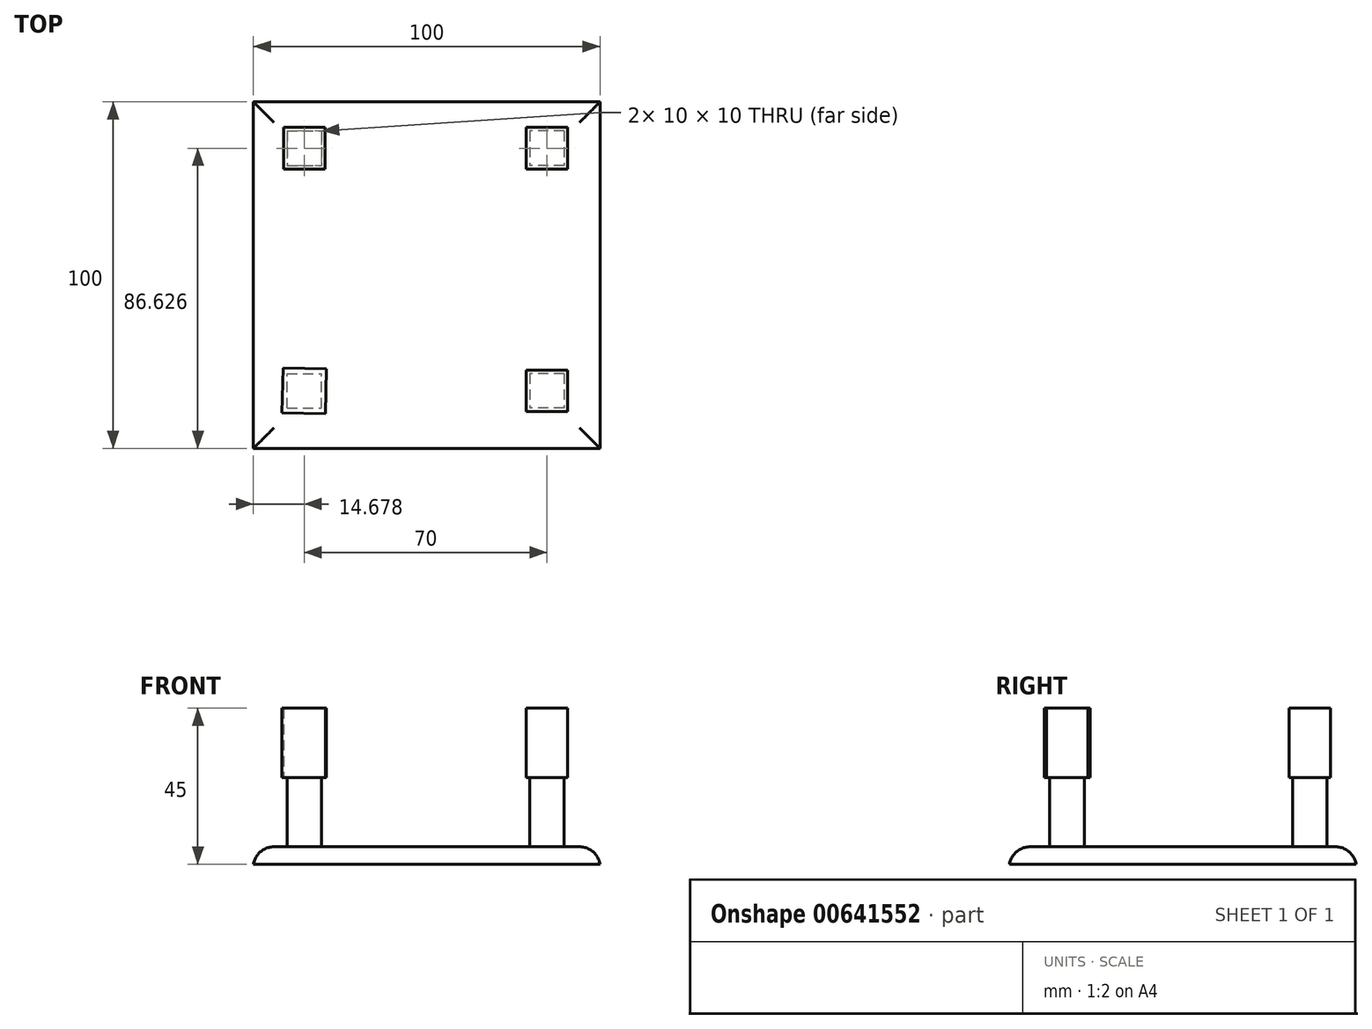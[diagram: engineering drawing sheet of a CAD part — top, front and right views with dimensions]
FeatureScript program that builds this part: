
annotation { "Feature Type Name" : "Feature", "Feature Type Description" : "" }
export const myFeature = defineFeature(function(context is Context, id is Id, definition is map)
    precondition{}
    {
        {
            var Q0;
            Q0=qCreatedBy(makeId("Top.planeOp"),FACE);
            var sketch = newSketch(context, id + "F0", { "sketchPlane" : qUnion([Q0])});
            skLineSegment(sketch, "E0.bottom", {"start": v(0, 0) * mm, "end": v(50, 0) * mm});
            skLineSegment(sketch, "E0.top", {"start": v(0, 50) * mm, "end": v(50, 50) * mm});
            skLineSegment(sketch, "E0.left", {"start": v(0, 0) * mm, "end": v(0, 50) * mm});
            skLineSegment(sketch, "E0.right", {"start": v(50, 0) * mm, "end": v(50, 50) * mm});
            skLineSegment(sketch, "E1.bottom", {"start": v(0, 0) * mm, "end": v(-50, 0) * mm});
            skLineSegment(sketch, "E1.top", {"start": v(0, 50) * mm, "end": v(-50, 50) * mm});
            skLineSegment(sketch, "E1.right", {"start": v(-50, 0) * mm, "end": v(-50, 50) * mm});
            skLineSegment(sketch, "E2.top", {"start": v(0, -50) * mm, "end": v(-50, -50) * mm});
            skLineSegment(sketch, "E2.left", {"start": v(0, 0) * mm, "end": v(0, -50) * mm});
            skLineSegment(sketch, "E2.right", {"start": v(-50, 0) * mm, "end": v(-50, -50) * mm});
            skLineSegment(sketch, "E3.top", {"start": v(0, -50) * mm, "end": v(50, -50) * mm});
            skLineSegment(sketch, "E3.right", {"start": v(50, 0) * mm, "end": v(50, -50) * mm});
            skSolve(sketch);
        }
        {
            var Q0;
            Q0 = qSketchRegion(id + "F0", true);
            extrude(context, id + "F1", {"entities" : qUnion([Q0]), "depth" : 5 * mm, "offsetDistance" : 25 * mm});
        }
        {
            var Q0;
            Q0=makeQuery(id+"F1.opExtrude","CAP_EDGE",EDGE,{"disambiguationData":[OSD([sQuery(id+"F0.wireOp",EDGE,"E1.right"),sQuery(id+"F0.wireOp",EDGE,"E2.right")])],"isStart":false});
            var Q1;
            Q1=makeQuery(id+"F1.opExtrude","CAP_EDGE",EDGE,{"disambiguationData":[OSD([sQuery(id+"F0.wireOp",EDGE,"E0.top"),sQuery(id+"F0.wireOp",EDGE,"E1.top")])],"isStart":false});
            var Q2;
            Q2=makeQuery(id+"F1.opExtrude","CAP_EDGE",EDGE,{"disambiguationData":[OSD([sQuery(id+"F0.wireOp",EDGE,"E0.right"),sQuery(id+"F0.wireOp",EDGE,"E3.right")])],"isStart":false});
            var Q3;
            Q3=makeQuery(id+"F1.opExtrude","CAP_EDGE",EDGE,{"disambiguationData":[OSD([sQuery(id+"F0.wireOp",EDGE,"E2.top"),sQuery(id+"F0.wireOp",EDGE,"E3.top")])],"isStart":false});
            fillet(context, id + "F2", {"entities" : qUnion([Q0, Q1, Q2, Q3]), "radius" : 6 * mm, "tangentPropagation" : true, "allowEdgeOverflow" : false});
        }
        {
            var Q0;
            Q0=qCreatedBy(makeId("Top.planeOp"),FACE);
            var sketch = newSketch(context, id + "F3", { "sketchPlane" : qUnion([Q0])});
            skLineSegment(sketch, "E4.bottom", {"start": v(-30.32, 31.63) * mm, "end": v(-40.32, 31.63) * mm});
            skLineSegment(sketch, "E4.top", {"start": v(-30.32, 41.63) * mm, "end": v(-40.32, 41.63) * mm});
            skLineSegment(sketch, "E4.left", {"start": v(-30.32, 31.63) * mm, "end": v(-30.32, 41.63) * mm});
            skLineSegment(sketch, "E4.right", {"start": v(-40.32, 31.63) * mm, "end": v(-40.32, 41.63) * mm});
            skPoint(sketch, "E4.middle", {"position": v(-35.32, 36.63) * mm});
            skLineSegment(sketch, "E5.bottom", {"start": v(-30.32, -28.37) * mm, "end": v(-40.32, -28.37) * mm});
            skLineSegment(sketch, "E5.top", {"start": v(-30.32, -38.37) * mm, "end": v(-40.32, -38.37) * mm});
            skLineSegment(sketch, "E5.left", {"start": v(-30.32, -28.37) * mm, "end": v(-30.32, -38.37) * mm});
            skLineSegment(sketch, "E5.right", {"start": v(-40.32, -28.37) * mm, "end": v(-40.32, -38.37) * mm});
            skPoint(sketch, "E5.middle", {"position": v(-35.32, -33.37) * mm});
            skPoint(sketch, "E5.middle.positionSnap0", {"position": v(-35.32, 31.63) * mm});
            skPoint(sketch, "E5.centerSnap0", {"position": v(-35.32, 31.63) * mm});
            skLineSegment(sketch, "E6.bottom", {"start": v(29.68, -38.37) * mm, "end": v(39.68, -38.37) * mm});
            skLineSegment(sketch, "E6.top", {"start": v(29.68, -28.37) * mm, "end": v(39.68, -28.37) * mm});
            skLineSegment(sketch, "E6.left", {"start": v(29.68, -38.37) * mm, "end": v(29.68, -28.37) * mm});
            skLineSegment(sketch, "E6.right", {"start": v(39.68, -38.37) * mm, "end": v(39.68, -28.37) * mm});
            skLineSegment(sketch, "E7.bottom", {"start": v(29.68, 31.63) * mm, "end": v(39.68, 31.63) * mm});
            skLineSegment(sketch, "E7.top", {"start": v(29.68, 41.63) * mm, "end": v(39.68, 41.63) * mm});
            skLineSegment(sketch, "E7.left", {"start": v(29.68, 31.63) * mm, "end": v(29.68, 41.63) * mm});
            skLineSegment(sketch, "E7.right", {"start": v(39.68, 31.63) * mm, "end": v(39.68, 41.63) * mm});
            skSolve(sketch);
        }
        {
            var Q0;
            Q0 = qSketchRegion(id + "F3", true);
            extrude(context, id + "F4", {"entities" : qUnion([Q0]), "operationType" : NewBodyOperationType.ADD, "depth" : 25 * mm, "offsetDistance" : 25 * mm});
        }
        {
            var Q0;
            Q0=makeQuery(id+"F4.opExtrude","CAP_FACE",FACE,{"disambiguationData":[OSD([sQuery(id+"F3.wireOp",EDGE,"E5.bottom"),sQuery(id+"F3.wireOp",EDGE,"E5.top"),sQuery(id+"F3.wireOp",EDGE,"E5.left"),sQuery(id+"F3.wireOp",EDGE,"E5.right")])],"isStart":false});
            var sketch = newSketch(context, id + "F5", { "sketchPlane" : qUnion([Q0])});
            skLineSegment(sketch, "E8", {"start": v(-40.32, -38.37) * mm, "end": v(-41.74, -39.79) * mm});
            skLineSegment(sketch, "E9", {"start": v(-28.97, -27.02) * mm, "end": v(-30.38, -28.43) * mm});
            skLineSegment(sketch, "E10", {"start": v(-29.18, -40.01) * mm, "end": v(-30.32, -38.37) * mm});
            skLineSegment(sketch, "E11", {"start": v(-40.32, -28.37) * mm, "end": v(-41.47, -26.74) * mm});
            skLineSegment(sketch, "E12", {"start": v(-41.74, -39.79) * mm, "end": v(-41.47, -26.74) * mm});
            skLineSegment(sketch, "E13", {"start": v(-28.97, -27.02) * mm, "end": v(-41.47, -26.74) * mm});
            skLineSegment(sketch, "E14", {"start": v(-28.97, -27.02) * mm, "end": v(-29.18, -40.01) * mm});
            skLineSegment(sketch, "E15", {"start": v(-41.74, -39.79) * mm, "end": v(-29.18, -40.01) * mm});
            skSolve(sketch);
        }
        {
            var Q0;
            Q0 = qSketchRegion(id + "F5", true);
            extrude(context, id + "F6", {"entities" : qUnion([Q0]), "depth" : 20 * mm, "offsetDistance" : 25 * mm});
        }
        {
            var Q0;
            Q0=makeQuery(id+"F4.opExtrude","CAP_FACE",FACE,{"disambiguationData":[OSD([sQuery(id+"F3.wireOp",EDGE,"E6.bottom"),sQuery(id+"F3.wireOp",EDGE,"E6.top"),sQuery(id+"F3.wireOp",EDGE,"E6.left"),sQuery(id+"F3.wireOp",EDGE,"E6.right")])],"isStart":false});
            var sketch = newSketch(context, id + "F7", { "sketchPlane" : qUnion([Q0])});
            skLineSegment(sketch, "E16.bottom", {"start": v(28.68, -27.37) * mm, "end": v(40.68, -27.37) * mm});
            skLineSegment(sketch, "E16.top", {"start": v(28.68, -39.37) * mm, "end": v(40.68, -39.37) * mm});
            skLineSegment(sketch, "E16.left", {"start": v(28.68, -27.37) * mm, "end": v(28.68, -39.37) * mm});
            skLineSegment(sketch, "E16.right", {"start": v(40.68, -27.37) * mm, "end": v(40.68, -39.37) * mm});
            skPoint(sketch, "E16.middle", {"position": v(34.68, -33.37) * mm});
            skPoint(sketch, "E17.0.start.orphan", {"position": v(29.68, -28.37) * mm});
            skPoint(sketch, "E18.0.end.orphan", {"position": v(39.68, -28.37) * mm});
            skPoint(sketch, "E19.0.end.orphan", {"position": v(39.68, -38.37) * mm});
            skPoint(sketch, "E19.0.start.orphan", {"position": v(29.68, -38.37) * mm});
            skSolve(sketch);
        }
        {
            var Q0;
            Q0 = qSketchRegion(id + "F7", true);
            var Q1;
            Q1=makeQuery(id+"F1.opExtrude","CAP_FACE",FACE,{"disambiguationData":[OSD([sQuery(id+"F0.wireOp",EDGE,"E0.top"),sQuery(id+"F0.wireOp",EDGE,"E0.right"),sQuery(id+"F0.wireOp",EDGE,"E1.top"),sQuery(id+"F0.wireOp",EDGE,"E1.right"),sQuery(id+"F0.wireOp",EDGE,"E2.top"),sQuery(id+"F0.wireOp",EDGE,"E2.right"),sQuery(id+"F0.wireOp",EDGE,"E3.top"),sQuery(id+"F0.wireOp",EDGE,"E3.right")])],"isStart":false});
            extrude(context, id + "F8", {"entities" : qUnion([Q0, Q1]), "depth" : 20 * mm, "offsetDistance" : 25 * mm});
        }
        {
            var Q0;
            Q0=makeQuery(id+"F8.opExtrude","SWEPT_BODY",BODY,{"disambiguationData":[OSD([sQuery(id+"F0.wireOp",EDGE,"E0.top"),sQuery(id+"F0.wireOp",EDGE,"E0.right"),sQuery(id+"F0.wireOp",EDGE,"E1.top"),sQuery(id+"F0.wireOp",EDGE,"E1.right"),sQuery(id+"F0.wireOp",EDGE,"E2.top"),sQuery(id+"F0.wireOp",EDGE,"E2.right"),sQuery(id+"F0.wireOp",EDGE,"E3.top"),sQuery(id+"F0.wireOp",EDGE,"E3.right")])]});
            deleteBodies(context, id + "F9", {"entities" : qUnion([Q0])});
        }
        {
            var Q0;
            Q0=sQuery(id+"F7.wireOp",EDGE,"E16.right");
            var Q1;
            Q1=sQuery(id+"F7.wireOp",EDGE,"E16.top");
            var Q2;
            Q2=sQuery(id+"F7.wireOp",EDGE,"E16.left");
            var Q3;
            Q3=sQuery(id+"F7.wireOp",EDGE,"E16.bottom");
            extrude(context, id + "F10", {"bodyType" : ToolBodyType.SURFACE, "surfaceEntities" : qUnion([Q0, Q1, Q2, Q3]), "depth" : 20 * mm, "offsetDistance" : 25 * mm});
        }
        {
            var Q0;
            Q0=makeQuery(id+"F4.opExtrude","CAP_FACE",FACE,{"disambiguationData":[OSD([sQuery(id+"F3.wireOp",EDGE,"E7.bottom"),sQuery(id+"F3.wireOp",EDGE,"E7.top"),sQuery(id+"F3.wireOp",EDGE,"E7.left"),sQuery(id+"F3.wireOp",EDGE,"E7.right")])],"isStart":false});
            var sketch = newSketch(context, id + "F11", { "sketchPlane" : qUnion([Q0])});
            skLineSegment(sketch, "E20.bottom", {"start": v(28.68, 30.63) * mm, "end": v(40.68, 30.63) * mm});
            skLineSegment(sketch, "E20.top", {"start": v(28.68, 42.63) * mm, "end": v(40.68, 42.63) * mm});
            skLineSegment(sketch, "E20.left", {"start": v(28.68, 30.63) * mm, "end": v(28.68, 42.63) * mm});
            skLineSegment(sketch, "E20.right", {"start": v(40.68, 30.63) * mm, "end": v(40.68, 42.63) * mm});
            skPoint(sketch, "E20.middle", {"position": v(34.68, 36.63) * mm});
            skPoint(sketch, "E21.orphan", {"position": v(29.68, 31.63) * mm});
            skPoint(sketch, "E22.end.orphan", {"position": v(39.68, 41.63) * mm});
            skSolve(sketch);
        }
        {
            var Q0;
            Q0 = qSketchRegion(id + "F11", true);
            extrude(context, id + "F12", {"entities" : qUnion([Q0]), "operationType" : NewBodyOperationType.ADD, "depth" : 20 * mm, "offsetDistance" : 25 * mm});
        }
        {
            var Q0;
            Q0=makeQuery(id+"F4.opExtrude","CAP_FACE",FACE,{"disambiguationData":[OSD([sQuery(id+"F3.wireOp",EDGE,"E4.bottom"),sQuery(id+"F3.wireOp",EDGE,"E4.top"),sQuery(id+"F3.wireOp",EDGE,"E4.left"),sQuery(id+"F3.wireOp",EDGE,"E4.right")])],"isStart":false});
            var sketch = newSketch(context, id + "F13", { "sketchPlane" : qUnion([Q0])});
            skLineSegment(sketch, "E23.bottom", {"start": v(-29.32, 30.63) * mm, "end": v(-41.32, 30.63) * mm});
            skLineSegment(sketch, "E23.top", {"start": v(-29.32, 42.63) * mm, "end": v(-41.32, 42.63) * mm});
            skLineSegment(sketch, "E23.left", {"start": v(-29.32, 30.63) * mm, "end": v(-29.32, 42.63) * mm});
            skLineSegment(sketch, "E23.right", {"start": v(-41.32, 30.63) * mm, "end": v(-41.32, 42.63) * mm});
            skPoint(sketch, "E23.middle", {"position": v(-35.32, 36.63) * mm});
            skPoint(sketch, "E24.orphan", {"position": v(-30.32, 41.63) * mm});
            skPoint(sketch, "E25.end.orphan", {"position": v(-40.32, 31.63) * mm});
            skSolve(sketch);
        }
        {
            var Q0;
            Q0 = qSketchRegion(id + "F13", true);
            extrude(context, id + "F14", {"entities" : qUnion([Q0]), "operationType" : NewBodyOperationType.ADD, "depth" : 20 * mm, "offsetDistance" : 25 * mm});
        }
    });
